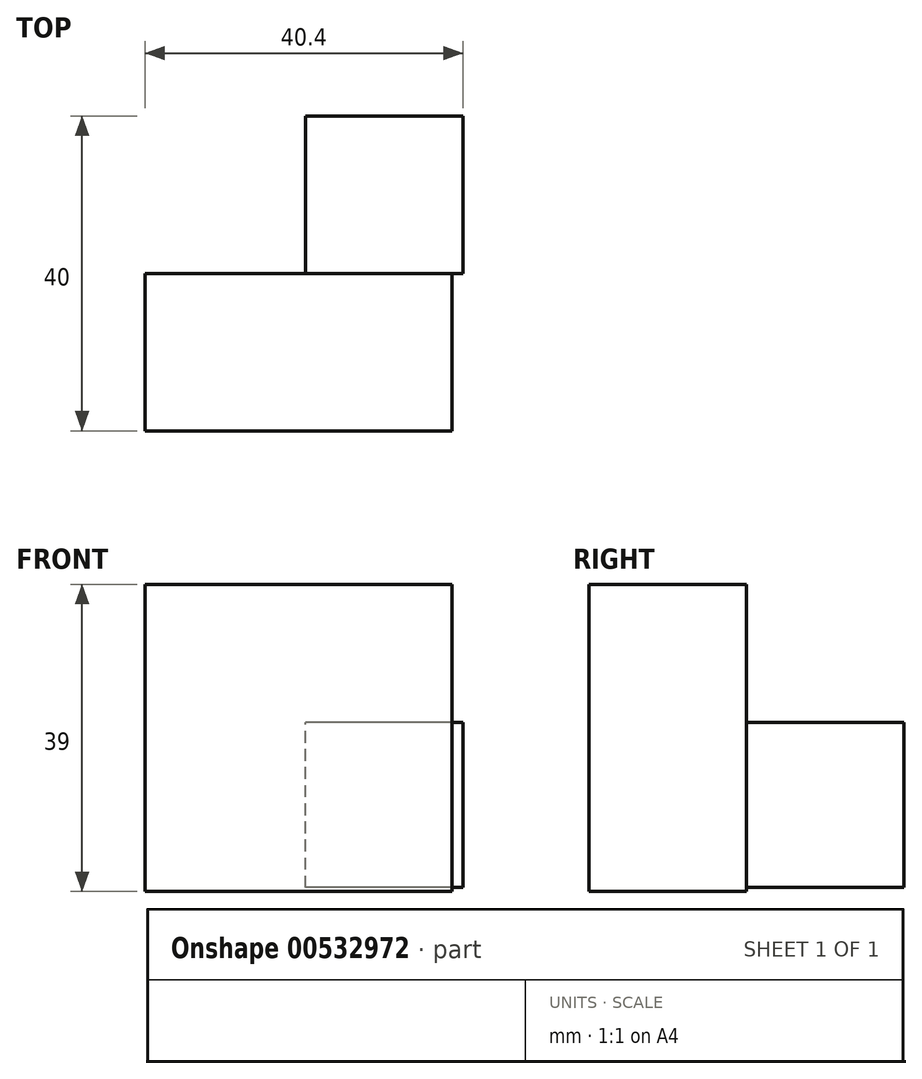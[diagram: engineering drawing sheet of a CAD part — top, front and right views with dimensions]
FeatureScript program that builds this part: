
annotation { "Feature Type Name" : "Feature", "Feature Type Description" : "" }
export const myFeature = defineFeature(function(context is Context, id is Id, definition is map)
    precondition{}
    {
        {
            var Q0;
            Q0=qCreatedBy(makeId("Front.planeOp"),FACE);
            var sketch = newSketch(context, id + "F0", { "sketchPlane" : qUnion([Q0])});
            skLineSegment(sketch, "E0.bottom", {"start": v(-20.4, 17.5) * mm, "end": v(18.6, 17.5) * mm});
            skLineSegment(sketch, "E0.top", {"start": v(-20.4, -21.5) * mm, "end": v(18.6, -21.5) * mm});
            skLineSegment(sketch, "E0.left", {"start": v(-20.4, 17.5) * mm, "end": v(-20.4, -21.5) * mm});
            skLineSegment(sketch, "E0.right", {"start": v(18.6, 17.5) * mm, "end": v(18.6, -21.5) * mm});
            skSolve(sketch);
        }
        {
            var Q0;
            Q0 = qSketchRegion(id + "F0", true);
            extrude(context, id + "F1", {"entities" : qUnion([Q0]), "depth" : 20 * mm, "offsetDistance" : 25 * mm});
        }
        {
            var Q0;
            Q0=qCreatedBy(makeId("Right.planeOp"),FACE);
            var sketch = newSketch(context, id + "F2", { "sketchPlane" : qUnion([Q0])});
            skLineSegment(sketch, "E1.left", {"start": v(0, 0) * mm, "end": v(0, -18.65) * mm});
            skLineSegment(sketch, "E2.bottom", {"start": v(0, -21) * mm, "end": v(20, -21) * mm});
            skLineSegment(sketch, "E2.top", {"start": v(0, 0) * mm, "end": v(20, 0) * mm});
            skLineSegment(sketch, "E2.left", {"start": v(0, -21) * mm, "end": v(0, 0) * mm});
            skLineSegment(sketch, "E2.right", {"start": v(20, -21) * mm, "end": v(20, 0) * mm});
            skSolve(sketch);
        }
        {
            var Q0;
            Q0 = qSketchRegion(id + "F2", true);
            extrude(context, id + "F3", {"entities" : qUnion([Q0]), "operationType" : NewBodyOperationType.ADD, "depth" : 20 * mm, "offsetDistance" : 25 * mm});
        }
    });
